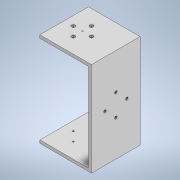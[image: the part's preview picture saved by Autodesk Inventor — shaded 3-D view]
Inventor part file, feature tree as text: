
AUTODESK INVENTOR PART (.ipt)
format: ipt  version: 2022.2 (Build 262287030, 287C)  size: 176,128 bytes
history: native  units: in
note: dims shown in document units (in); Inventor stores cm internally (conversion verified against a paired STEP export)
features: sketch x4, hole x3, extrude x1
ambient origin geometry x8: Origin, YZ Plane, XZ Plane, XY Plane, X Axis, Y Axis, Z Axis, Center Point
bodies: Solid1 (feature_tree)
feature tree (8):
  extrude  "Extrusion1"  TaperAngle=90.0deg  [1 undecoded]
  sketch  "Sketch3"  dims[d2=3.1496in d3=90.0deg]
  hole  "Hole2"  [1 undecoded]
  hole  "Hole3"  [1 undecoded]
  hole  "Hole4"  [1 undecoded]
  sketch  "Sketch1"  dims[d0=5.7087in d1=90.0deg]
  sketch  "Sketch5"  dims[d4=0.1969in d5=90.0deg]
  sketch  "Sketch6"  dims[d6=3.3465in d7=90.0deg d8=6.1024in d9=90.0deg d10=3.3465in d11=90.0deg d12=0.1969in d13=90.0deg d14=3.1496in d15=0.0in d30=90.0deg d31=2.1654in d32=1.5748in d33=0.5906in d34=1.5748in d36=360.0deg d38=0.0968in d39=0.2362in d40=0.2362in d41=0.0394in d42=90.0deg d43=0.3937in d44=0.8108in d45=2.8543in d48=90.0deg d49=2.1654in d50=0.5906in d51=1.5748in d53=360.0deg d55=0.0968in d56=0.2362in d57=0.2362in d58=0.0394in d59=90.0deg d60=0.3937in d61=0.0in d62=0.7098in d63=1.5748in d65=360.0deg d67=0.1628in d68=0.3937in d69=0.3909in d70=0.0787in d71=90.0deg d72=0.3937in d73=0.0in d46=0.8108in d47=0.0246in d64=0.3937in d66=0.0984in]
note: 4 required parameter values undecoded (feature->parameter linkage not recoverable at this tier; creation-order binding heuristic only, values carry confidence <= 0.55)
